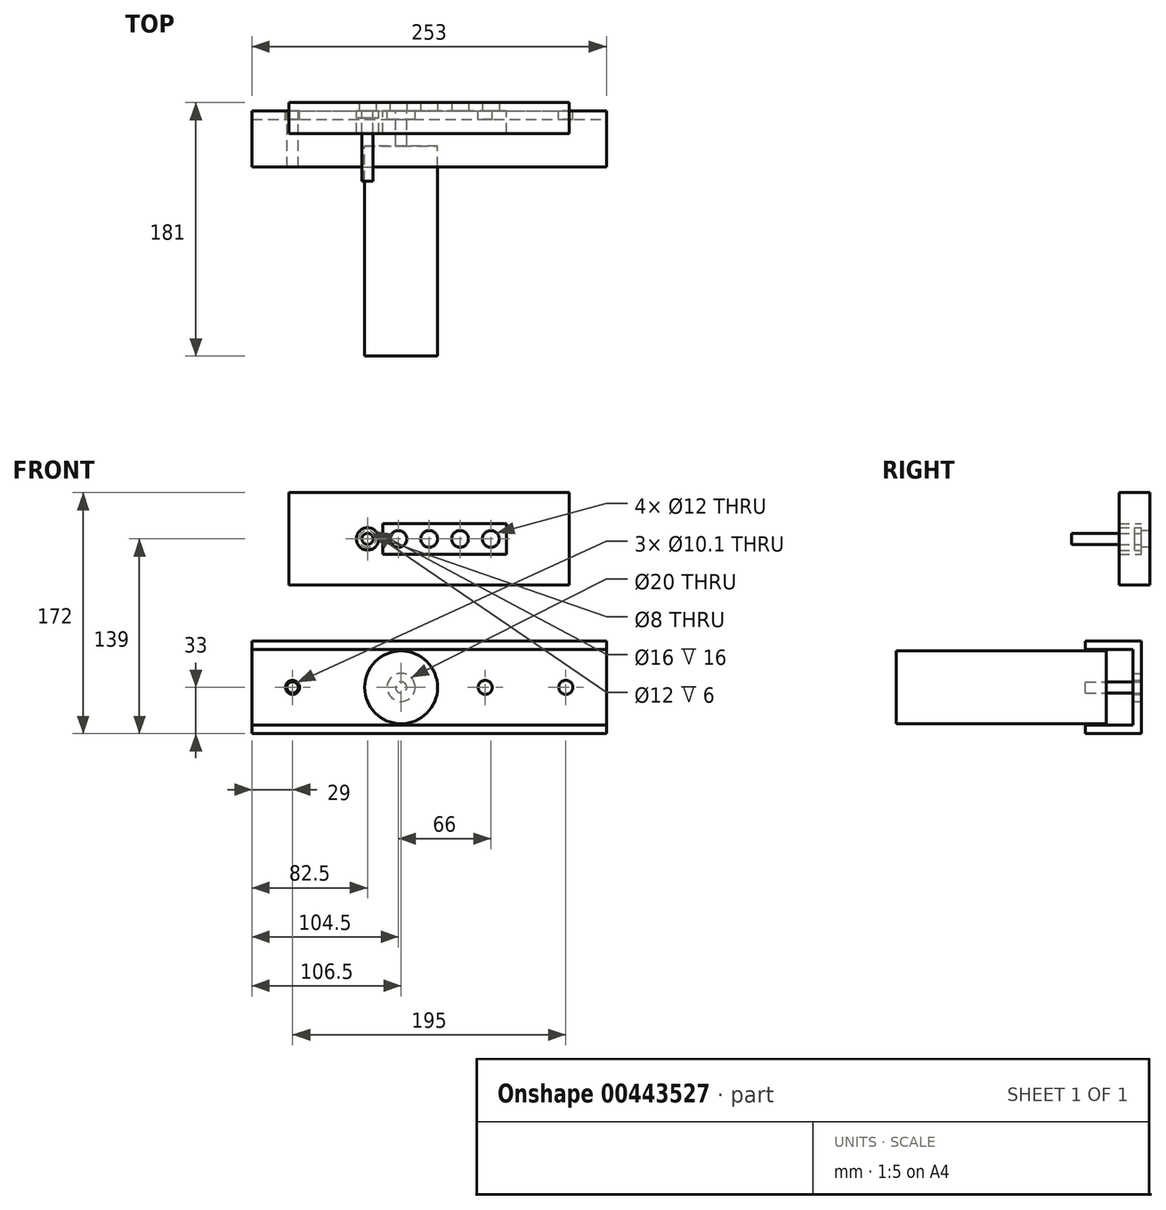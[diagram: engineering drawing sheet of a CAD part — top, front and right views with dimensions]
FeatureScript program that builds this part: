
annotation { "Feature Type Name" : "Feature", "Feature Type Description" : "" }
export const myFeature = defineFeature(function(context is Context, id is Id, definition is map)
    precondition{}
    {
        {
            var Q0;
            Q0=qCreatedBy(makeId("Front.planeOp"),FACE);
            var sketch = newSketch(context, id + "F0", { "sketchPlane" : qUnion([Q0])});
            skLineSegment(sketch, "E0.bottom", {"start": v(-126.5, 33) * mm, "end": v(126.5, 33) * mm});
            skLineSegment(sketch, "E0.top", {"start": v(-126.5, -33) * mm, "end": v(126.5, -33) * mm});
            skLineSegment(sketch, "E0.left", {"start": v(-126.5, 33) * mm, "end": v(-126.5, -33) * mm});
            skLineSegment(sketch, "E0.right", {"start": v(126.5, 33) * mm, "end": v(126.5, -33) * mm});
            skPoint(sketch, "E0.middle", {"position": v(0, 0) * mm});
            skCircle(sketch, "E1", {"center": v(-20, 0) * mm, "radius": 10 * mm});
            skCircle(sketch, "E2", {"center": v(-97.5, 0) * mm, "radius": 5.05 * mm});
            skCircle(sketch, "E3", {"center": v(97.5, 0) * mm, "radius": 5.05 * mm});
            skLineSegment(sketch, "E4", {"start": v(-126.5, 27) * mm, "end": v(126.5, 27) * mm});
            skLineSegment(sketch, "E5", {"start": v(-126.5, -27) * mm, "end": v(126.5, -27) * mm});
            skCircle(sketch, "E6", {"center": v(-97.5, 0) * mm, "radius": 4 * mm});
            skCircle(sketch, "E7", {"center": v(-20, 0) * mm, "radius": 1.59 * mm});
            skLineSegment(sketch, "E8.bottom", {"start": v(-100, 139) * mm, "end": v(100, 139) * mm});
            skLineSegment(sketch, "E8.top", {"start": v(-100, 73) * mm, "end": v(100, 73) * mm});
            skLineSegment(sketch, "E8.left", {"start": v(-100, 139) * mm, "end": v(-100, 73) * mm});
            skLineSegment(sketch, "E8.right", {"start": v(100, 139) * mm, "end": v(100, 73) * mm});
            skPoint(sketch, "E8.middle", {"position": v(0, 106) * mm});
            skCircle(sketch, "E9", {"center": v(0, 106) * mm, "radius": 8 * mm});
            skCircle(sketch, "E10", {"center": v(22, 106) * mm, "radius": 8 * mm});
            skCircle(sketch, "E11", {"center": v(44, 106) * mm, "radius": 8 * mm});
            skCircle(sketch, "E12", {"center": v(-22, 106) * mm, "radius": 8 * mm});
            skCircle(sketch, "E13", {"center": v(-44, 106) * mm, "radius": 8 * mm});
            skLineSegment(sketch, "E14", {"start": v(44, 106) * mm, "end": v(22, 106) * mm, "construction": true});
            skLineSegment(sketch, "E15", {"start": v(22, 106) * mm, "end": v(0, 106) * mm, "construction": true});
            skLineSegment(sketch, "E16", {"start": v(0, 106) * mm, "end": v(-22, 106) * mm, "construction": true});
            skLineSegment(sketch, "E17", {"start": v(-22, 106) * mm, "end": v(-44, 106) * mm, "construction": true});
            skLineSegment(sketch, "E18.bottom", {"start": v(-33, 95) * mm, "end": v(-55, 95) * mm});
            skLineSegment(sketch, "E18.top", {"start": v(-33, 117) * mm, "end": v(-55, 117) * mm});
            skLineSegment(sketch, "E18.left", {"start": v(-33, 95) * mm, "end": v(-33, 117) * mm});
            skLineSegment(sketch, "E18.right", {"start": v(-55, 95) * mm, "end": v(-55, 117) * mm});
            skLineSegment(sketch, "E19.bottom", {"start": v(-33, 95) * mm, "end": v(-11, 95) * mm});
            skLineSegment(sketch, "E19.top", {"start": v(-33, 117) * mm, "end": v(-11, 117) * mm});
            skLineSegment(sketch, "E19.right", {"start": v(-11, 95) * mm, "end": v(-11, 117) * mm});
            skLineSegment(sketch, "E20.bottom", {"start": v(-11, 95) * mm, "end": v(11, 95) * mm});
            skLineSegment(sketch, "E20.top", {"start": v(-11, 117) * mm, "end": v(11, 117) * mm});
            skLineSegment(sketch, "E20.right", {"start": v(11, 95) * mm, "end": v(11, 117) * mm});
            skLineSegment(sketch, "E21.bottom", {"start": v(11, 95) * mm, "end": v(33, 95) * mm});
            skLineSegment(sketch, "E21.top", {"start": v(11, 117) * mm, "end": v(33, 117) * mm});
            skLineSegment(sketch, "E21.right", {"start": v(33, 95) * mm, "end": v(33, 117) * mm});
            skLineSegment(sketch, "E22.bottom", {"start": v(33, 95) * mm, "end": v(55, 95) * mm});
            skLineSegment(sketch, "E22.top", {"start": v(33, 117) * mm, "end": v(55, 117) * mm});
            skLineSegment(sketch, "E22.right", {"start": v(55, 95) * mm, "end": v(55, 117) * mm});
            skCircle(sketch, "E23", {"center": v(-44, 106) * mm, "radius": 4 * mm});
            skCircle(sketch, "E24", {"center": v(-22, 106) * mm, "radius": 6 * mm});
            skCircle(sketch, "E25", {"center": v(0, 106) * mm, "radius": 6 * mm});
            skCircle(sketch, "E26", {"center": v(22, 106) * mm, "radius": 6 * mm});
            skCircle(sketch, "E27", {"center": v(44, 106) * mm, "radius": 6 * mm});
            skCircle(sketch, "E28", {"center": v(-44, 106) * mm, "radius": 6 * mm});
            skCircle(sketch, "E29", {"center": v(40, 0) * mm, "radius": 5.05 * mm});
            skLineSegment(sketch, "E30", {"start": v(0, 0) * mm, "end": v(-97.5, 0) * mm, "construction": true});
            skLineSegment(sketch, "E31", {"start": v(0, 0) * mm, "end": v(97.5, 0) * mm, "construction": true});
            skSolve(sketch);
        }
        {
            var Q0;
            Q0=makeQuery(id+"F0.imprint","IMPRINT",FACE,{"disambiguationData":[TD([[makeQuery(id+"F0.imprint","IMPRINT",EDGE,{"derivedFrom":sQuery(id+"F0.wireOp",EDGE,"sf6jrUsn-nWUX-B3Fb-vJeZ-nCy09vWzX1Ch")}),-1.0]])]});
            var Q1;
            Q1=makeQuery(id+"F0.imprint","IMPRINT",FACE,{"disambiguationData":[TD([[makeQuery(id+"F0.imprint","IMPRINT",EDGE,{"derivedFrom":sQuery(id+"F0.wireOp",EDGE,"E8.bottom")}),-1.0]])]});
            var Q2;
            Q2=makeQuery(id+"F0.imprint","IMPRINT",FACE,{"disambiguationData":[TD([[makeQuery(id+"F0.imprint","IMPRINT",EDGE,{"derivedFrom":sQuery(id+"F0.wireOp",EDGE,"E18.bottom")}),1.0]])]});
            var Q3;
            {var subQ0=sQuery(id+"F0.wireOp",EDGE,"E8.top");Q3=makeQuery(id+"F0.imprint","IMPRINT",FACE,{"disambiguationData":[TD([[makeQuery(id+"F0.imprint","IMPRINT",EDGE,{"derivedFrom":subQ0}),1.0]])]});}
            extrude(context, id + "F1", {"entities" : qUnion([Q0, Q1, Q2, Q3]), "depth" : 16 * mm});
        }
        {
            var Q0;
            Q0=makeQuery(id+"F0.imprint","IMPRINT",FACE,{"disambiguationData":[TD([[makeQuery(id+"F0.imprint","IMPRINT",EDGE,{"derivedFrom":sQuery(id+"F0.wireOp",EDGE,"E1")}),-1.0]])]});
            extrude(context, id + "F2", {"entities" : qUnion([Q0]), "depth" : 6 * mm});
        }
        {
            var Q0;
            {var subQ0=sQuery(id+"F0.wireOp",EDGE,"E0.bottom");Q0=makeQuery(id+"F0.imprint","IMPRINT",FACE,{"disambiguationData":[TD([[makeQuery(id+"F0.imprint","IMPRINT",EDGE,{"derivedFrom":subQ0}),-1.0]])]});}
            var Q1;
            {var subQ0=sQuery(id+"F0.wireOp",EDGE,"E0.top");Q1=makeQuery(id+"F0.imprint","IMPRINT",FACE,{"disambiguationData":[TD([[makeQuery(id+"F0.imprint","IMPRINT",EDGE,{"derivedFrom":subQ0}),1.0]])]});}
            extrude(context, id + "F3", {"entities" : qUnion([Q0, Q1]), "operationType" : NewBodyOperationType.ADD, "depth" : 40 * mm});
        }
        {
            var Q0;
            Q0=makeQuery(id+"F0.imprint","IMPRINT",FACE,{"disambiguationData":[TD([[makeQuery(id+"F0.imprint","IMPRINT",EDGE,{"derivedFrom":sQuery(id+"F0.wireOp",EDGE,"E6")}),1.0]])]});
            extrude(context, id + "F4", {"entities" : qUnion([Q0]), "depth" : 40 * mm});
        }
        {
            var Q0;
            {var subQ0=sQuery(id+"F0.wireOp",EDGE,"E8.top");Q0=makeQuery(id+"F0.imprint","IMPRINT",FACE,{"disambiguationData":[TD([[makeQuery(id+"F0.imprint","IMPRINT",EDGE,{"derivedFrom":subQ0}),1.0]])]});}
            var sketch = newSketch(context, id + "F5", { "sketchPlane" : qUnion([Q0])});
            skCircle(sketch, "E32", {"center": v(-20, 0) * mm, "radius": 4 * mm});
            skSolve(sketch);
        }
        {
            var Q0;
            Q0=makeQuery(id+"F5.imprint","IMPRINT",FACE,{"disambiguationData":[TD([[makeQuery(id+"F5.imprint","IMPRINT",EDGE,{"derivedFrom":sQuery(id+"F5.wireOp",EDGE,"E32")}),1.0]])]});
            var Q1;
            Q1=makeQuery(id+"F5.imprint","IMPRINT",FACE,{"disambiguationData":[TD([[makeQuery(id+"F5.imprint","IMPRINT",EDGE,{"derivedFrom":makeQuery(id+"FFGbZArmiwniyhI_0.opExtrude","CAP_EDGE",EDGE,{"disambiguationData":[OSD([sQuery(id+"F0.wireOp",EDGE,"E7")])],"isStart":false})}),1.0]])]});
            extrude(context, id + "F6", {"entities" : qUnion([Q0, Q1]), "depth" : 25 * mm});
        }
        {
            var Q0;
            Q0=makeQuery(id+"F6.opExtrude","CAP_FACE",FACE,{"disambiguationData":[OSD([sQuery(id+"F5.wireOp",EDGE,"E32")])],"isStart":false});
            var sketch = newSketch(context, id + "F7", { "sketchPlane" : qUnion([Q0])});
            skCircle(sketch, "E33", {"center": v(-20, 0) * mm, "radius": 26 * mm});
            skSolve(sketch);
        }
        {
            var Q0;
            Q0=qSketchRegion(id+"F7",true);
            extrude(context, id + "F8", {"entities" : qUnion([Q0]), "operationType" : NewBodyOperationType.ADD, "depth" : (185 - 35) * mm});
        }
        {
            var Q0;
            Q0=makeQuery(id+"F0.imprint","IMPRINT",FACE,{"disambiguationData":[TD([[makeQuery(id+"F0.imprint","IMPRINT",EDGE,{"derivedFrom":sQuery(id+"F0.wireOp",EDGE,"E13")}),-1.0]])]});
            var Q1;
            Q1=makeQuery(id+"F1.opExtrude","CAP_FACE",FACE,{"disambiguationData":[OSD([sQuery(id+"F0.wireOp",EDGE,"E8.bottom"),sQuery(id+"F0.wireOp",EDGE,"E8.top"),sQuery(id+"F0.wireOp",EDGE,"E8.left"),sQuery(id+"F0.wireOp",EDGE,"E8.right"),sQuery(id+"F0.wireOp",EDGE,"E18.bottom"),sQuery(id+"F0.wireOp",EDGE,"E18.top"),sQuery(id+"F0.wireOp",EDGE,"E18.right"),sQuery(id+"F0.wireOp",EDGE,"E19.bottom"),sQuery(id+"F0.wireOp",EDGE,"E19.top"),sQuery(id+"F0.wireOp",EDGE,"E20.bottom"),sQuery(id+"F0.wireOp",EDGE,"E20.top"),sQuery(id+"F0.wireOp",EDGE,"E21.bottom"),sQuery(id+"F0.wireOp",EDGE,"E21.top"),sQuery(id+"F0.wireOp",EDGE,"E22.bottom"),sQuery(id+"F0.wireOp",EDGE,"E22.top"),sQuery(id+"F0.wireOp",EDGE,"E22.right")])],"isStart":false});
            var Q2;
            Q2=makeQuery(id+"F1.opExtrude","CAP_FACE",FACE,{"disambiguationData":[OSD([sQuery(id+"F0.wireOp",EDGE,"E8.bottom"),sQuery(id+"F0.wireOp",EDGE,"E8.top"),sQuery(id+"F0.wireOp",EDGE,"E8.left"),sQuery(id+"F0.wireOp",EDGE,"E8.right"),sQuery(id+"F0.wireOp",EDGE,"E18.bottom"),sQuery(id+"F0.wireOp",EDGE,"E18.top"),sQuery(id+"F0.wireOp",EDGE,"E18.right"),sQuery(id+"F0.wireOp",EDGE,"E19.bottom"),sQuery(id+"F0.wireOp",EDGE,"E19.top"),sQuery(id+"F0.wireOp",EDGE,"E20.bottom"),sQuery(id+"F0.wireOp",EDGE,"E20.top"),sQuery(id+"F0.wireOp",EDGE,"E21.bottom"),sQuery(id+"F0.wireOp",EDGE,"E21.top"),sQuery(id+"F0.wireOp",EDGE,"E22.bottom"),sQuery(id+"F0.wireOp",EDGE,"E22.top"),sQuery(id+"F0.wireOp",EDGE,"E22.right")])],"isStart":true});
            extrude(context, id + "F9", {"entities" : qUnion([Q0]), "endBound" : BoundingType.UP_TO_SURFACE, "endBoundEntityFace" : qUnion([Q1]), "depth" : 25 * mm});
        }
        {
            var Q0;
            Q0=makeQuery(id+"F0.imprint","IMPRINT",FACE,{"disambiguationData":[TD([[makeQuery(id+"F0.imprint","IMPRINT",EDGE,{"derivedFrom":sQuery(id+"F0.wireOp",EDGE,"E18.bottom")}),1.0]])]});
            var Q1;
            {var subQ0=sQuery(id+"F0.wireOp",EDGE,"E8.bottom");Q1=makeQuery(id+"F0.imprint","IMPRINT",FACE,{"disambiguationData":[TD([[makeQuery(id+"F0.imprint","IMPRINT",EDGE,{"derivedFrom":subQ0}),-1.0]])]});}
            var Q2;
            Q2=makeQuery(id+"F0.imprint","IMPRINT",FACE,{"disambiguationData":[TD([[makeQuery(id+"F0.imprint","IMPRINT",EDGE,{"derivedFrom":sQuery(id+"F0.wireOp",EDGE,"E13")}),-1.0]])]});
            var Q3;
            Q3=makeQuery(id+"F0.imprint","IMPRINT",FACE,{"disambiguationData":[TD([[makeQuery(id+"F0.imprint","IMPRINT",EDGE,{"derivedFrom":sQuery(id+"F0.wireOp",EDGE,"E12")}),-1.0]])]});
            var Q4;
            Q4=makeQuery(id+"F0.imprint","IMPRINT",FACE,{"disambiguationData":[TD([[makeQuery(id+"F0.imprint","IMPRINT",EDGE,{"derivedFrom":sQuery(id+"F0.wireOp",EDGE,"E9")}),-1.0]])]});
            var Q5;
            Q5=makeQuery(id+"F0.imprint","IMPRINT",FACE,{"disambiguationData":[TD([[makeQuery(id+"F0.imprint","IMPRINT",EDGE,{"derivedFrom":sQuery(id+"F0.wireOp",EDGE,"E10")}),-1.0]])]});
            var Q6;
            Q6=makeQuery(id+"F0.imprint","IMPRINT",FACE,{"disambiguationData":[TD([[makeQuery(id+"F0.imprint","IMPRINT",EDGE,{"derivedFrom":sQuery(id+"F0.wireOp",EDGE,"E11")}),-1.0]])]});
            var Q7;
            Q7=makeQuery(id+"F0.imprint","IMPRINT",FACE,{"disambiguationData":[TD([[makeQuery(id+"F0.imprint","IMPRINT",EDGE,{"derivedFrom":sQuery(id+"F0.wireOp",EDGE,"E11")}),1.0]])]});
            var Q8;
            Q8=makeQuery(id+"F0.imprint","IMPRINT",FACE,{"disambiguationData":[TD([[makeQuery(id+"F0.imprint","IMPRINT",EDGE,{"derivedFrom":sQuery(id+"F0.wireOp",EDGE,"E10")}),1.0]])]});
            var Q9;
            Q9=makeQuery(id+"F0.imprint","IMPRINT",FACE,{"disambiguationData":[TD([[makeQuery(id+"F0.imprint","IMPRINT",EDGE,{"derivedFrom":sQuery(id+"F0.wireOp",EDGE,"E9")}),1.0]])]});
            var Q10;
            Q10=makeQuery(id+"F0.imprint","IMPRINT",FACE,{"disambiguationData":[TD([[makeQuery(id+"F0.imprint","IMPRINT",EDGE,{"derivedFrom":sQuery(id+"F0.wireOp",EDGE,"E12")}),1.0]])]});
            var Q11;
            Q11=makeQuery(id+"F0.imprint","IMPRINT",FACE,{"disambiguationData":[TD([[makeQuery(id+"F0.imprint","IMPRINT",EDGE,{"derivedFrom":sQuery(id+"F0.wireOp",EDGE,"E13")}),1.0]])]});
            var Q12;
            {var subQ0=sQuery(id+"F0.wireOp",EDGE,"E8.top");Q12=makeQuery(id+"F0.imprint","IMPRINT",FACE,{"disambiguationData":[TD([[makeQuery(id+"F0.imprint","IMPRINT",EDGE,{"derivedFrom":subQ0}),1.0]])]});}
            extrude(context, id + "F10", {"entities" : qUnion([Q0, Q1, Q2, Q3, Q4, Q5, Q6, Q7, Q8, Q9, Q10, Q11, Q12]), "operationType" : NewBodyOperationType.ADD, "oppositeDirection" : true, "depth" : 6 * mm});
        }
        {
            var Q0;
            Q0=makeQuery(id+"F0.imprint","IMPRINT",FACE,{"disambiguationData":[TD([[makeQuery(id+"F0.imprint","IMPRINT",EDGE,{"derivedFrom":sQuery(id+"F0.wireOp",EDGE,"E13")}),1.0]])]});
            var Q1;
            Q1=makeQuery(id+"F0.imprint","IMPRINT",FACE,{"disambiguationData":[TD([[makeQuery(id+"F0.imprint","IMPRINT",EDGE,{"derivedFrom":sQuery(id+"F0.wireOp",EDGE,"E23")}),-1.0]])]});
            extrude(context, id + "F11", {"entities" : qUnion([Q0, Q1]), "depth" : 5 * mm});
        }
        {
            var Q0;
            Q0=makeQuery(id+"F0.imprint","IMPRINT",FACE,{"disambiguationData":[TD([[makeQuery(id+"F0.imprint","IMPRINT",EDGE,{"derivedFrom":sQuery(id+"F0.wireOp",EDGE,"E23")}),1.0]])]});
            extrude(context, id + "F12", {"entities" : qUnion([Q0]), "depth" : 50 * mm});
        }
    });
